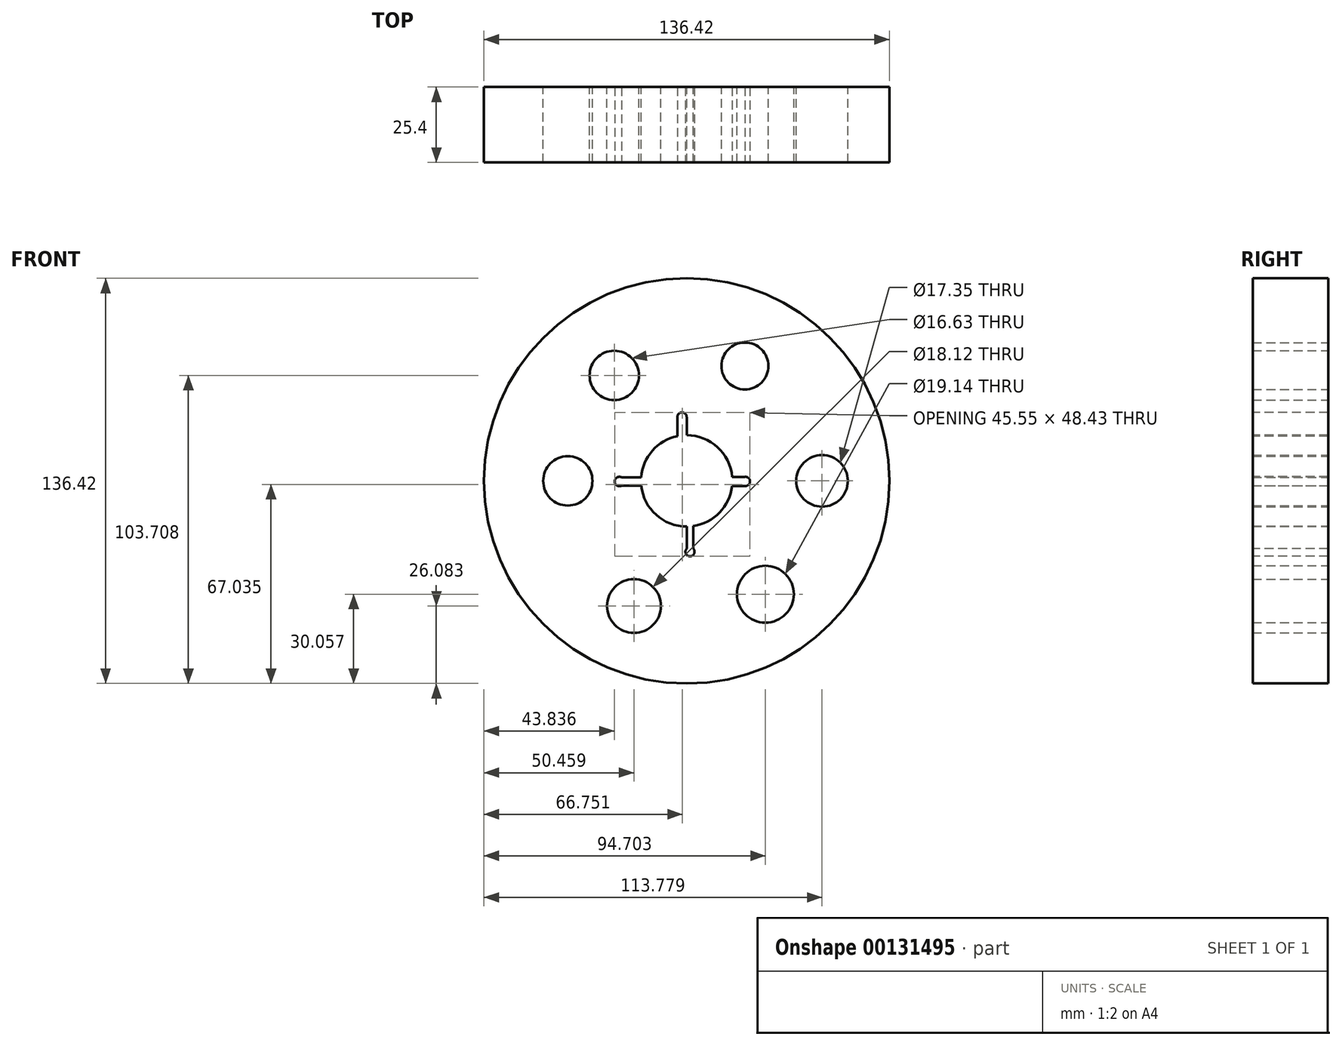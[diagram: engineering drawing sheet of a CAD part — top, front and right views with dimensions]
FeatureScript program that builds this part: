
annotation { "Feature Type Name" : "Feature", "Feature Type Description" : "" }
export const myFeature = defineFeature(function(context is Context, id is Id, definition is map)
    precondition{}
    {
        {
            var Q0;
            Q0=qCreatedBy(makeId("Front.planeOp"),FACE);
            var sketch = newSketch(context, id + "F0", { "sketchPlane" : qUnion([Q0])});
            skCircle(sketch, "E0", {"center": v(0, 0) * mm, "radius": 68.21 * mm});
            skCircle(sketch, "E1", {"center": v(0, 0) * mm, "radius": 15.38 * mm});
            skCircle(sketch, "E2", {"center": v(-40, 0) * mm, "radius": 8.3 * mm});
            skCircle(sketch, "E3", {"center": v(45.57, 0) * mm, "radius": 8.68 * mm});
            skCircle(sketch, "E4", {"center": v(-24.37, 35.5) * mm, "radius": 8.31 * mm});
            skCircle(sketch, "E5", {"center": v(19.6, 38.68) * mm, "radius": 7.9 * mm});
            skCircle(sketch, "E6", {"center": v(-17.75, -42.13) * mm, "radius": 9.06 * mm});
            skCircle(sketch, "E7", {"center": v(26.5, -38.15) * mm, "radius": 9.57 * mm});
            skSolve(sketch);
        }
        {
            var Q0;
            Q0 = qSketchRegion(id + "F0", true);
            extrude(context, id + "F1", {"entities" : qUnion([Q0]), "depth" : 25.4 * mm});
        }
        {
            var Q0;
            Q0=makeQuery(id+"F1.opExtrude","CAP_FACE",FACE,{"disambiguationData":[OSD([sQuery(id+"F0.wireOp",EDGE,"E0"),sQuery(id+"F0.wireOp",EDGE,"E1"),sQuery(id+"F0.wireOp",EDGE,"E2"),sQuery(id+"F0.wireOp",EDGE,"E3"),sQuery(id+"F0.wireOp",EDGE,"E4"),sQuery(id+"F0.wireOp",EDGE,"E5"),sQuery(id+"F0.wireOp",EDGE,"E6"),sQuery(id+"F0.wireOp",EDGE,"E7")])],"isStart":false});
            var sketch = newSketch(context, id + "F2", { "sketchPlane" : qUnion([Q0])});
            skLineSegment(sketch, "E8", {"start": v(-3.17, 15.05) * mm, "end": v(-3.17, 21.46) * mm});
            skLineSegment(sketch, "E9", {"start": v(-3.17, 21.46) * mm, "end": v(0, 21.46) * mm});
            skLineSegment(sketch, "E10", {"start": v(0, 21.46) * mm, "end": v(0, 15.38) * mm});
            skLineSegment(sketch, "E11", {"start": v(0, 15.38) * mm, "end": v(-3.17, 15.05) * mm});
            skArc(sketch, "E12", {"start": v(0, 21.46) * mm, "mid": v(-1.58, 23.04) * mm, "end": v(-3.17, 21.46) * mm});
            skSolve(sketch);
        }
        {
            var Q0;
            Q0 = qSketchRegion(id + "F2", true);
            extrude(context, id + "F3", {"entities" : qUnion([Q0]), "operationType" : NewBodyOperationType.REMOVE, "endBound" : BoundingType.THROUGH_ALL, "oppositeDirection" : true, "depth" : 25.4 * mm});
        }
        {
            var Q0;
            Q0=makeQuery(id+"F1.opExtrude","CAP_FACE",FACE,{"disambiguationData":[OSD([sQuery(id+"F0.wireOp",EDGE,"E0"),sQuery(id+"F0.wireOp",EDGE,"E1"),sQuery(id+"F0.wireOp",EDGE,"E2"),sQuery(id+"F0.wireOp",EDGE,"E3"),sQuery(id+"F0.wireOp",EDGE,"E4"),sQuery(id+"F0.wireOp",EDGE,"E5"),sQuery(id+"F0.wireOp",EDGE,"E6"),sQuery(id+"F0.wireOp",EDGE,"E7")])],"isStart":false});
            var sketch = newSketch(context, id + "F4", { "sketchPlane" : qUnion([Q0])});
            skLineSegment(sketch, "E13", {"start": v(15.32, 1.38) * mm, "end": v(19.6, 1.38) * mm});
            skLineSegment(sketch, "E14", {"start": v(15.32, 1.38) * mm, "end": v(13.76, 0) * mm});
            skLineSegment(sketch, "E15", {"start": v(13.76, 0) * mm, "end": v(15.28, -1.71) * mm});
            skLineSegment(sketch, "E16", {"start": v(15.28, -1.71) * mm, "end": v(19.77, -1.71) * mm});
            skLineSegment(sketch, "E17", {"start": v(-13.78, 1.38) * mm, "end": v(-13.78, 0) * mm});
            skLineSegment(sketch, "E18", {"start": v(-13.78, 0) * mm, "end": v(-13.78, -1.62) * mm});
            skLineSegment(sketch, "E19", {"start": v(-13.78, -1.62) * mm, "end": v(-21.95, -1.62) * mm});
            skLineSegment(sketch, "E20", {"start": v(-21.95, -1.62) * mm, "end": v(-21.95, 1.22) * mm});
            skLineSegment(sketch, "E21", {"start": v(-21.95, 1.22) * mm, "end": v(-13.44, 1.22) * mm});
            skLineSegment(sketch, "E22", {"start": v(-13.44, 1.22) * mm, "end": v(-13.78, -1.62) * mm});
            skLineSegment(sketch, "E23", {"start": v(-1.76, -13.64) * mm, "end": v(2.25, -13.64) * mm});
            skLineSegment(sketch, "E24", {"start": v(2.25, -13.64) * mm, "end": v(2.25, -22.82) * mm});
            skLineSegment(sketch, "E25", {"start": v(2.25, -22.82) * mm, "end": v(0, -22.82) * mm});
            skLineSegment(sketch, "E26", {"start": v(0, -22.82) * mm, "end": v(0, -13.64) * mm});
            skArc(sketch, "E27", {"start": v(-21.95, 1.22) * mm, "mid": v(-24.24, -0.2) * mm, "end": v(-21.95, -1.62) * mm});
            skArc(sketch, "E28", {"start": v(0, -22.82) * mm, "mid": v(1.12, -25.4) * mm, "end": v(2.25, -22.82) * mm});
            skArc(sketch, "E29", {"start": v(19.77, -1.71) * mm, "mid": v(21.32, -0.08) * mm, "end": v(19.6, 1.38) * mm});
            skSolve(sketch);
        }
        {
            var Q0;
            Q0 = qSketchRegion(id + "F4", true);
            extrude(context, id + "F5", {"entities" : qUnion([Q0]), "operationType" : NewBodyOperationType.REMOVE, "endBound" : BoundingType.THROUGH_ALL, "oppositeDirection" : true, "depth" : 25.4 * mm});
        }
    });
